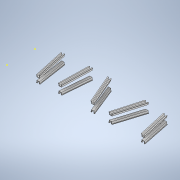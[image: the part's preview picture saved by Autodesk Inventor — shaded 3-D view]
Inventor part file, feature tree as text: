
AUTODESK INVENTOR PART (.ipt)
format: ipt  version: 2022 (Build 260153000, 153)  size: 728,064 bytes
history: native  units: mm
features: sketch x28, loft x10, plane x1
ambient origin geometry x8: Origin, YZ Plane, XZ Plane, XY Plane, X Axis, Y Axis, Z Axis, Center Point
bodies: Body1 (feature_tree)
feature tree (39):
  sketch  "Sketch3"  dims[d29=150.0mm d35=2.0mm]
  sketch  "Sketch4"  dims[d36=90.0deg d37=2.0mm]
  sketch  "Sketch5"  dims[d38=90.0deg d43=2.0mm]
  sketch  "Sketch6"  dims[d44=2.0mm d51=2.0mm]
  plane  "Work Plane2"
  sketch  "Sketch9"  dims[d52=2.0mm d56=2.0mm]
  sketch  "Sketch10"  dims[d57=2.0mm d65=2.0mm]
  sketch  "Sketch14"  dims[d66=2.0mm d69=2.0mm]
  sketch  "Sketch15"  dims[d70=2.0mm d76=2.0mm]
  sketch  "Sketch16"  dims[d77=0.0mm d150=1.8mm]
  sketch  "Sketch17"  dims[d151=1.8mm d156=1.8mm]
  sketch  "Sketch18"  dims[d157=1.8mm]
  sketch  "Sketch19"  dims[d167=1.8mm]
  sketch  "Sketch20"  dims[d168=90.0deg]
  sketch  "Sketch21"  dims[d169=1.8mm]
  sketch  "Sketch22"  dims[d170=90.0deg]
  sketch  "Sketch23"  dims[d175=1.8mm]
  sketch  "Sketch24"  dims[d176=1.8mm]
  sketch  "Sketch25"  dims[d187=1.8mm]
  sketch  "Sketch26"  dims[d188=1.8mm]
  sketch  "Sketch27"  dims[d193=1.8mm]
  sketch  "Sketch28"  dims[d194=90.0deg]
  sketch  "Sketch29"  dims[d195=1.8mm]
  sketch  "Sketch30"  dims[d196=90.0deg]
  sketch  "Sketch31"  dims[d203=25.0mm]
  sketch  "Sketch32"  dims[d204=25.0mm]
  sketch  "Sketch33"  dims[d205=25.0mm d206=25.0mm]
  sketch  "Sketch34"  dims[d207=25.0mm d208=25.0mm]
  sketch  "Sketch35"  dims[d209=25.0mm d210=25.0mm d211=25.0mm d212=25.0mm d213=25.0mm d214=25.0mm d215=25.0mm d216=25.0mm d217=25.0mm d218=25.0mm d219=25.0mm d220=25.0mm d221=25.0mm d222=25.0mm d223=25.0mm d224=25.0mm d225=25.0mm d226=25.0mm d227=25.0mm d228=25.0mm d229=25.0mm d230=25.0mm d231=25.0mm d232=25.0mm d233=25.0mm d234=25.0mm d235=25.0mm d236=25.0mm d237=25.0mm d238=25.0mm d239=25.0mm d240=25.0mm d241=25.0mm d242=25.0mm d245=5.0mm d250=2.0mm d253=5.0mm d254=5.0mm d257=2.0mm d273=2.0mm d281=2.0mm d293=2.0mm d301=2.0mm d310=2.0mm d318=2.0mm d324=2.0mm d337=2.0mm d340=5.0mm d343=2.0mm d349=2.0mm d351=5.0mm d352=5.0mm d356=2.0mm d364=2.0mm d365=10.0mm d366=5.0mm d367=5.0mm d373=2.0mm d383=2.0mm d394=2.0mm d405=2.0mm d412=2.0mm d415=5.0mm d421=2.0mm d422=0.0mm d423=90.0deg d424=0.0mm d425=90.0deg d426=0.0mm d427=90.0deg d428=0.0mm d429=90.0deg d430=0.0mm d431=90.0deg d432=0.0mm d433=90.0deg d434=0.0mm d435=90.0deg d436=0.0mm d437=90.0deg d438=0.0mm d439=90.0deg d440=0.0mm d441=90.0deg d442=0.0mm d443=90.0deg d444=0.0mm d445=90.0deg d446=0.0mm d447=90.0deg d448=0.0mm d449=90.0deg d450=0.0mm d451=90.0deg d452=0.0mm d453=90.0deg d454=0.0mm d455=90.0deg d456=0.0mm d457=90.0deg d458=0.0mm d459=90.0deg d460=0.0mm d461=90.0deg d6=0.5mm d7=0.872665mm d8=0.5mm d9=0.872665mm]
  loft  "Loft2"
  loft  "Loft3"
  loft  "Loft4"
  loft  "Loft5"
  loft  "Loft6"
  loft  "Loft7"
  loft  "Loft8"
  loft  "Loft9"
  loft  "Loft10"
  loft  "Loft11"
